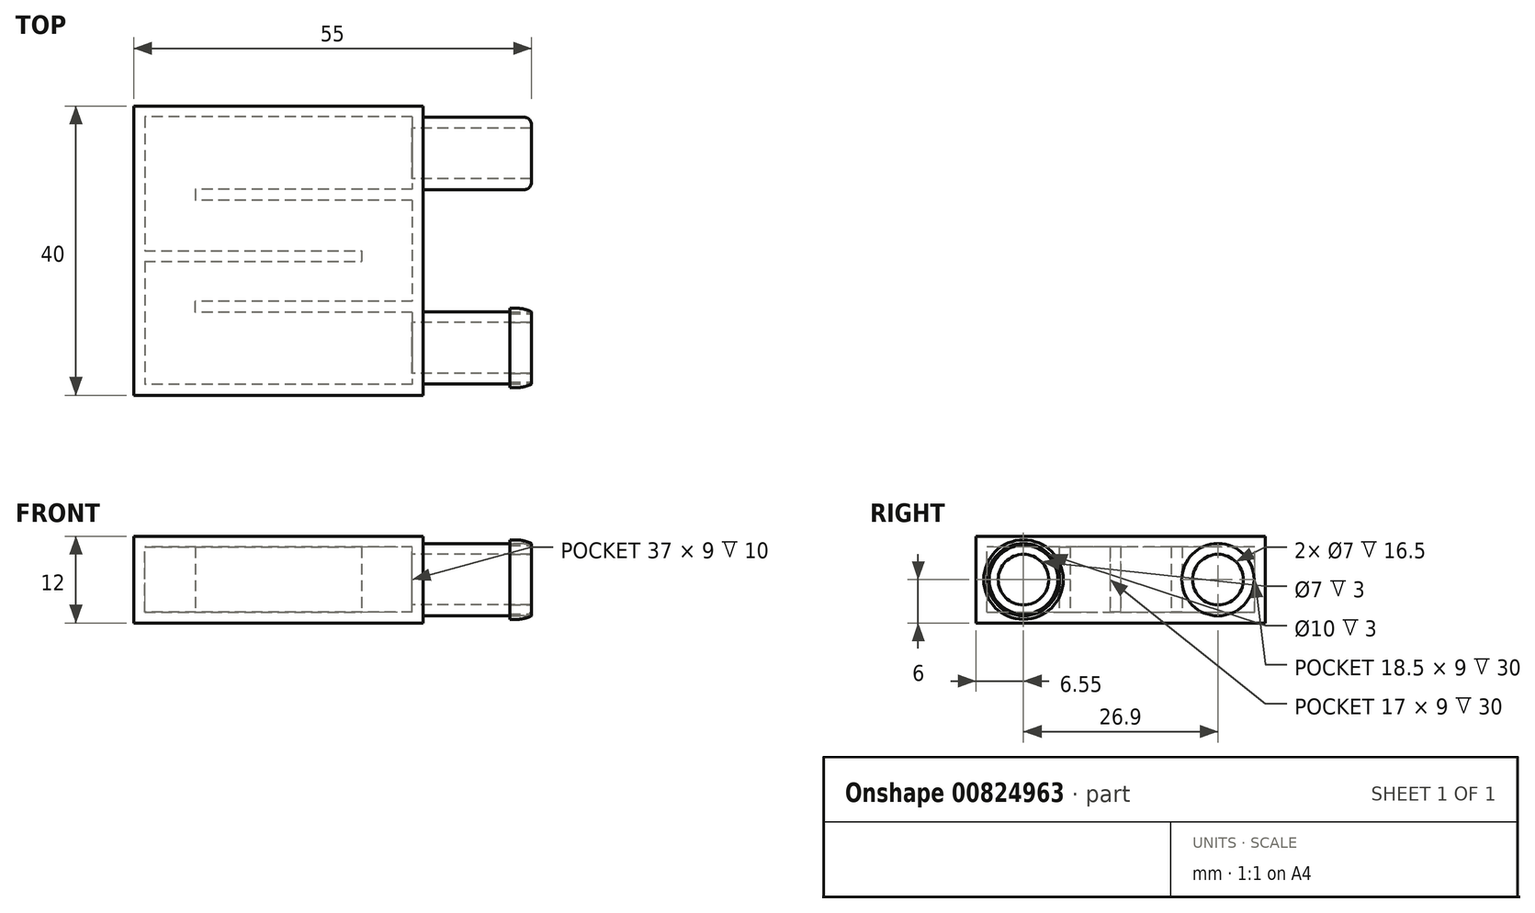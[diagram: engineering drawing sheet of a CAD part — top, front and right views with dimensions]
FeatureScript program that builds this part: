
annotation { "Feature Type Name" : "Feature", "Feature Type Description" : "" }
export const myFeature = defineFeature(function(context is Context, id is Id, definition is map)
    precondition{}
    {
        {
            var Q0;
            Q0=qCreatedBy(makeId("Right.planeOp"),FACE);
            var sketch = newSketch(context, id + "F0", { "sketchPlane" : qUnion([Q0])});
            skLineSegment(sketch, "E0.bottom", {"start": v(0, 0) * mm, "end": v(40, 0) * mm});
            skLineSegment(sketch, "E0.top", {"start": v(0, 12) * mm, "end": v(40, 12) * mm});
            skLineSegment(sketch, "E0.left", {"start": v(0, 0) * mm, "end": v(0, 12) * mm});
            skLineSegment(sketch, "E0.right", {"start": v(40, 0) * mm, "end": v(40, 12) * mm});
            skLineSegment(sketch, "E1", {"start": v(20, 17.6) * mm, "end": v(20, -7.3) * mm, "construction": true});
            skPoint(sketch, "E1.startSnap0", {"position": v(20, 12) * mm});
            skLineSegment(sketch, "E2", {"start": v(-4.14, 6) * mm, "end": v(51.5, 6) * mm, "construction": true});
            skPoint(sketch, "E2.startSnap0", {"position": v(0, 6) * mm});
            skSolve(sketch);
        }
        {
            var Q0;
            Q0=makeQuery(id+"F0.imprint","IMPRINT",FACE,{"disambiguationData":[TD([[makeQuery(id+"F0.imprint","IMPRINT",EDGE,{"derivedFrom":sQuery(id+"F0.wireOp",EDGE,"E0.bottom")}),1.0]])]});
            extrude(context, id + "F1", {"entities" : qUnion([Q0]), "depth" : 40 * mm, "offsetDistance" : 25 * mm});
        }
        {
            var Q0;
            Q0=makeQuery(id+"F1.opExtrude","SWEPT_FACE",FACE,{"disambiguationData":[OSD([sQuery(id+"F0.wireOp",EDGE,"E0.top")])]});
            shell(context, id + "F2", {"entities" : qUnion([Q0]), "thickness" : 1.5 * mm});
        }
        {
            var Q0;
            Q0=makeQuery(id+"F1.opExtrude","CAP_FACE",FACE,{"disambiguationData":[OSD([sQuery(id+"F0.wireOp",EDGE,"E0.bottom"),sQuery(id+"F0.wireOp",EDGE,"E0.top"),sQuery(id+"F0.wireOp",EDGE,"E0.left"),sQuery(id+"F0.wireOp",EDGE,"E0.right")])],"isStart":false});
            var sketch = newSketch(context, id + "F3", { "sketchPlane" : qUnion([Q0])});
            skLineSegment(sketch, "E3", {"start": v(0, 6) * mm, "end": v(46.52, 6) * mm, "construction": true});
            skLineSegment(sketch, "E4", {"start": v(20, 14.2) * mm, "end": v(20, -3.55) * mm, "construction": true});
            skPoint(sketch, "E4.startSnap0", {"position": v(20, 12) * mm});
            skPoint(sketch, "E4.endSnap0", {"position": v(20, 0) * mm});
            skCircle(sketch, "E5", {"center": v(6.55, 6) * mm, "radius": 5 * mm});
            skCircle(sketch, "E6.MirrorC", {"center": v(33.45, 6) * mm, "radius": 5 * mm});
            skSolve(sketch);
        }
        {
            var Q0;
            Q0 = qSketchRegion(id + "F3", true);
            extrude(context, id + "F4", {"entities" : qUnion([Q0]), "operationType" : NewBodyOperationType.ADD, "depth" : 15 * mm, "offsetDistance" : 25 * mm});
        }
        {
            var Q0;
            Q0=makeQuery(id+"F4.opExtrude","CAP_FACE",FACE,{"disambiguationData":[OSD([sQuery(id+"F3.wireOp",EDGE,"E5")])],"isStart":false});
            var Q1;
            Q1=makeQuery(id+"F4.opExtrude","CAP_FACE",FACE,{"disambiguationData":[OSD([sQuery(id+"F3.wireOp",EDGE,"E6.MirrorC")])],"isStart":false});
            shell(context, id + "F5", {"entities" : qUnion([Q0, Q1]), "thickness" : 1.5 * mm});
        }
        {
            var Q0;
            Q0=makeQuery(id+"F5.opShell","OFFSET_FACE",FACE,{"disambiguationData":[OSD([sQuery(id+"F0.wireOp",EDGE,"E0.bottom"),sQuery(id+"F0.wireOp",EDGE,"E0.top"),sQuery(id+"F0.wireOp",EDGE,"E0.left"),sQuery(id+"F0.wireOp",EDGE,"E0.right")]),OD(0.0)]});
            var Q1;
            Q1=makeQuery(id+"F5.opShell","OFFSET_FACE",FACE,{"disambiguationData":[OSD([sQuery(id+"F0.wireOp",EDGE,"E0.bottom"),sQuery(id+"F0.wireOp",EDGE,"E0.top"),sQuery(id+"F0.wireOp",EDGE,"E0.left"),sQuery(id+"F0.wireOp",EDGE,"E0.right")]),OD(1.0)]});
            extrude(context, id + "F6", {"entities" : qUnion([Q0, Q1]), "operationType" : NewBodyOperationType.REMOVE, "oppositeDirection" : true, "depth" : 5 * mm, "offsetDistance" : 25 * mm});
        }
        {
            var Q0;
            Q0=makeQuery(id+"F2.opShell","OFFSET_FACE",FACE,{"disambiguationData":[OSD([sQuery(id+"F0.wireOp",EDGE,"E0.bottom")])]});
            var sketch = newSketch(context, id + "F7", { "sketchPlane" : qUnion([Q0])});
            skLineSegment(sketch, "E7.bottom", {"start": v(38.5, 11.5) * mm, "end": v(8.5, 11.5) * mm});
            skLineSegment(sketch, "E7.top", {"start": v(38.5, 13) * mm, "end": v(8.5, 13) * mm});
            skLineSegment(sketch, "E7.left", {"start": v(38.5, 11.5) * mm, "end": v(38.5, 13) * mm});
            skLineSegment(sketch, "E7.right", {"start": v(8.5, 11.5) * mm, "end": v(8.5, 13) * mm});
            skLineSegment(sketch, "E8.bottom", {"start": v(38.5, 28.5) * mm, "end": v(8.5, 28.5) * mm});
            skLineSegment(sketch, "E8.top", {"start": v(38.5, 27) * mm, "end": v(8.5, 27) * mm});
            skLineSegment(sketch, "E8.left", {"start": v(38.5, 28.5) * mm, "end": v(38.5, 27) * mm});
            skLineSegment(sketch, "E8.right", {"start": v(8.5, 28.5) * mm, "end": v(8.5, 27) * mm});
            skLineSegment(sketch, "E9.bottom", {"start": v(1.5, 20) * mm, "end": v(31.5, 20) * mm});
            skLineSegment(sketch, "E9.top", {"start": v(1.5, 18.5) * mm, "end": v(31.5, 18.5) * mm});
            skLineSegment(sketch, "E9.left", {"start": v(1.5, 20) * mm, "end": v(1.5, 18.5) * mm});
            skLineSegment(sketch, "E9.right", {"start": v(31.5, 20) * mm, "end": v(31.5, 18.5) * mm});
            skSolve(sketch);
        }
        {
            var Q0;
            Q0 = qSketchRegion(id + "F7", true);
            extrude(context, id + "F8", {"entities" : qUnion([Q0]), "operationType" : NewBodyOperationType.ADD, "depth" : 10.5 * mm, "offsetDistance" : 25 * mm});
        }
        {
            var Q0;
            Q0=makeQuery(id+"F8.boolean.opBoolean","MERGE",FACE,{"derivedFrom":[makeQuery(id+"F1.opExtrude","SWEPT_FACE",FACE,{"disambiguationData":[OSD([sQuery(id+"F0.wireOp",EDGE,"E0.top")])]}),makeQuery(id+"F8.opExtrude","CAP_FACE",FACE,{"disambiguationData":[OSD([sQuery(id+"F7.wireOp",EDGE,"E7.bottom"),sQuery(id+"F7.wireOp",EDGE,"E7.top"),sQuery(id+"F7.wireOp",EDGE,"E7.left"),sQuery(id+"F7.wireOp",EDGE,"E7.right")])],"isStart":false}),makeQuery(id+"F8.opExtrude","CAP_FACE",FACE,{"disambiguationData":[OSD([sQuery(id+"F7.wireOp",EDGE,"E8.bottom"),sQuery(id+"F7.wireOp",EDGE,"E8.top"),sQuery(id+"F7.wireOp",EDGE,"E8.left"),sQuery(id+"F7.wireOp",EDGE,"E8.right")])],"isStart":false}),makeQuery(id+"F8.opExtrude","CAP_FACE",FACE,{"disambiguationData":[OSD([sQuery(id+"F7.wireOp",EDGE,"E9.bottom"),sQuery(id+"F7.wireOp",EDGE,"E9.top"),sQuery(id+"F7.wireOp",EDGE,"E9.left"),sQuery(id+"F7.wireOp",EDGE,"E9.right")])],"isStart":false})]});
            var sketch = newSketch(context, id + "F9", { "sketchPlane" : qUnion([Q0])});
            skLineSegment(sketch, "E10.bottom", {"start": v(0, 40) * mm, "end": v(40, 40) * mm});
            skLineSegment(sketch, "E10.top", {"start": v(0, 0) * mm, "end": v(40, 0) * mm});
            skLineSegment(sketch, "E10.left", {"start": v(0, 40) * mm, "end": v(0, 0) * mm});
            skLineSegment(sketch, "E10.right", {"start": v(40, 40) * mm, "end": v(40, 0) * mm});
            skSolve(sketch);
        }
        {
            var Q0;
            Q0 = qSketchRegion(id + "F9", true);
            extrude(context, id + "F10", {"entities" : qUnion([Q0]), "operationType" : NewBodyOperationType.ADD, "oppositeDirection" : true, "depth" : 1.5 * mm, "offsetDistance" : 25 * mm});
        }
        {
            var Q0;
            Q0=makeQuery(id+"F4.opExtrude","CAP_FACE",FACE,{"disambiguationData":[OSD([sQuery(id+"F3.wireOp",EDGE,"E5")])],"isStart":false});
            var sketch = newSketch(context, id + "F11", { "sketchPlane" : qUnion([Q0])});
            skCircle(sketch, "E11", {"center": v(6.55, 6) * mm, "radius": 5.5 * mm});
            skCircle(sketch, "E12", {"center": v(6.55, 6) * mm, "radius": 4.74 * mm});
            skSolve(sketch);
        }
        {
            var Q0;
            Q0=makeQuery(id+"F11.imprint","IMPRINT",FACE,{"disambiguationData":[TD([[makeQuery(id+"F11.imprint","IMPRINT",EDGE,{"derivedFrom":sQuery(id+"F11.wireOp",EDGE,"E12")}),1.0]])]});
            var Q1;
            Q1=makeQuery(id+"F11.imprint","IMPRINT",FACE,{"disambiguationData":[TD([[makeQuery(id+"F11.imprint","IMPRINT",EDGE,{"derivedFrom":sQuery(id+"F11.wireOp",EDGE,"E11")}),1.0]])]});
            var Q2;
            Q2=sQuery(id+"F11.wireOp",EDGE,"E11");
            var Q3;
            Q3=sQuery(id+"F11.wireOp",EDGE,"E12");
            extrude(context, id + "F12", {"entities" : qUnion([Q0, Q1]), "surfaceEntities" : qUnion([Q2, Q3]), "oppositeDirection" : true, "depth" : 3 * mm, "offsetDistance" : 25 * mm});
        }
        {
            var Q0;
            Q0=makeQuery(id+"F12.opExtrude","CAP_EDGE",EDGE,{"disambiguationData":[OSD([sQuery(id+"F11.wireOp",EDGE,"E11")])],"isStart":true});
            fillet(context, id + "F13", {"entities" : qUnion([Q0]), "radius" : 5 * mm, "tangentPropagation" : true, "allowEdgeOverflow" : false});
        }
        {
            var Q0;
            Q0=makeQuery(id+"F4.opExtrude","CAP_EDGE",EDGE,{"disambiguationData":[OSD([sQuery(id+"F3.wireOp",EDGE,"E6.MirrorC")])],"isStart":false});
            fillet(context, id + "F14", {"entities" : qUnion([Q0]), "radius" : 1 * mm, "tangentPropagation" : true, "allowEdgeOverflow" : false});
        }
    });
